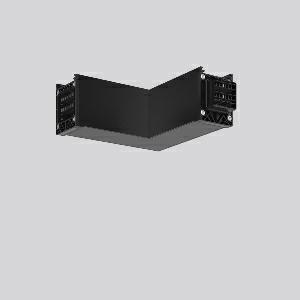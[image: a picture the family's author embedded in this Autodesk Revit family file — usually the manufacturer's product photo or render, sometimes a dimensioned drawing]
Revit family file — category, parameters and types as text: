
# Revit family: linedo_l-verbindung_982773_003_3_e0d6
name_source: partatom
category: Lighting Fixtures
units: mm (PartAtom-declared; Revit-internal decimal feet)

## family parameters
Cut with Voids When Loaded = No
Host = Face
Light Source = No
Part Type = Normal
Room Calculation Point = No
Round Connector Dimension = Use Diameter
Shared = No

## types (1)
- LINEDO L-Verbindung
    Apparent Load = 0 VA
    Default Elevation = 1800 mm
    Description = Series: LINEDO
L-connector, 14-pole, connection socket / plug. Housing: extruded aluminium profile, powder-coated. Cover made of plastic, surface like housing. LINEDO plug system, plastic, black. Easy connection for rigid or flexible wires. 2 membrane cable entries (M25). Suitable for power supply in 7-pole version. Ready prewired. Colour-coded individual cables enable easy electromechanical separation.
Colour: jet black (RAL 9005)
Length: 185 mm
Width: 204 mm
Height: 76 mm
Weight: 730 g
    Height = 76 mm
    Lamp = 0 x
    Length = 185 mm
    Luminous efficacy = 0 lm/W
    Manufacturer = RZB
    ModVariant = No
    Model = 982773.003.3
    Mounting Place = Ceiling
    Mounting Type = Surface mounted
    Number of Poles = 1
    OnlyDefault = Yes
    Power Factor = 1
    Product Name = LINEDO L-Verbindung
    Product group = Surface mounted continuous line luminaire system
    ProductGroupID = 310
    Protection Class = Protection class I
    Protection Degree = Degree of protection
    RLX_Detail_Level = 1
    RLX_Emergency_Light_Flux = 0 lm
    RLX_Emergency_Type = 0
    RLX_Emergency_Type_DB = No
    RlxData = <blob elided: 19101 chars, md5=22820b43>
    Standby Power = 0 W
    System Light Flux = 0 lm
    System Power = 0 W
    Type Comments = Product without accessories
    Type Image = 982773.003.3.jpg
    URL = http://relux.com
    VarID = ---
    Voltage = 0 V
    Weight = 0.00 kg
    Width = 204 mm

## geometry (parser evidence)
native form markers: Blend x4, Sweep x11
no freeform markers — native parametric forms only
